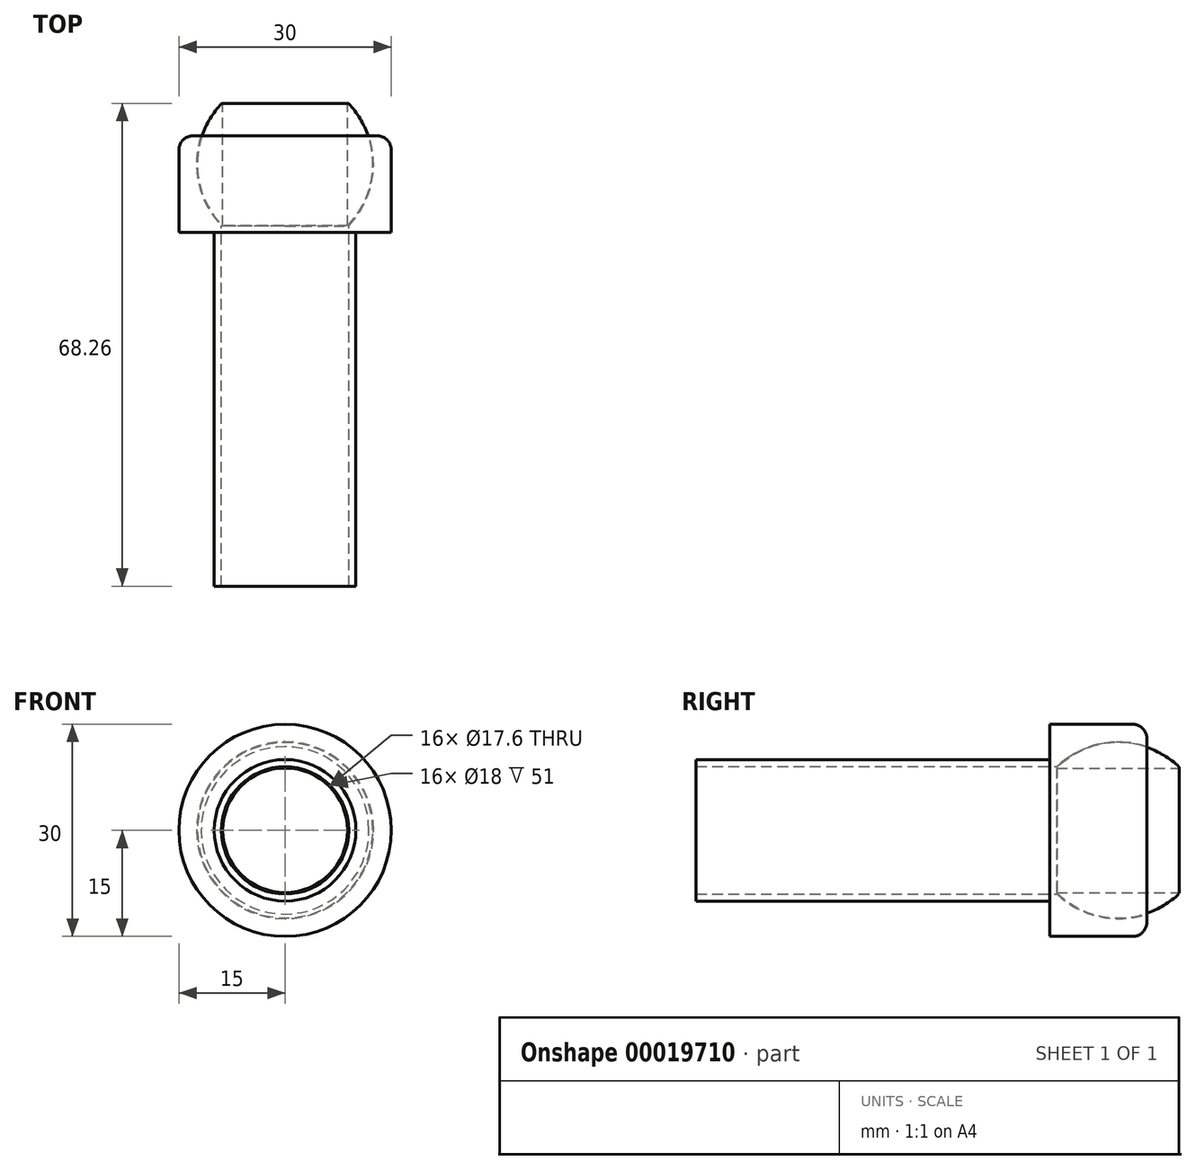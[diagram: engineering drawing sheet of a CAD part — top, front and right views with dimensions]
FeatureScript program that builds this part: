
annotation { "Feature Type Name" : "Feature", "Feature Type Description" : "" }
export const myFeature = defineFeature(function(context is Context, id is Id, definition is map)
    precondition{}
    {
        {
            var Q0;
            Q0=qCreatedBy(makeId("Top.planeOp"),FACE);
            var sketch = newSketch(context, id + "F0", { "sketchPlane" : qUnion([Q0])});
            skLineSegment(sketch, "E0", {"start": v(0, 31.42) * mm, "end": v(0, -28.3) * mm, "construction": true});
            skArc(sketch, "E1", {"start": v(9, 1) * mm, "mid": v(12.2, 6.95) * mm, "end": v(11.84, 13.69) * mm});
            skLineSegment(sketch, "E2", {"start": v(9, 0) * mm, "end": v(9, 1) * mm});
            skLineSegment(sketch, "E3", {"start": v(15, 0) * mm, "end": v(15, 13.69) * mm});
            skLineSegment(sketch, "E4", {"start": v(11.84, 13.69) * mm, "end": v(15, 13.69) * mm});
            skLineSegment(sketch, "E5", {"start": v(9, 0) * mm, "end": v(9, -50) * mm});
            skLineSegment(sketch, "E6", {"start": v(9, -50) * mm, "end": v(10, -50) * mm});
            skLineSegment(sketch, "E7", {"start": v(10, -50) * mm, "end": v(10, 0) * mm});
            skLineSegment(sketch, "E8", {"start": v(10, 0) * mm, "end": v(15, 0) * mm});
            skArc(sketch, "E9", {"start": v(8.8, 0.94) * mm, "mid": v(12.4, 9.67) * mm, "end": v(8.8, 18.41) * mm});
            skLineSegment(sketch, "E10", {"start": v(8.8, 19.95) * mm, "end": v(8.8, -2.87) * mm});
            skSolve(sketch);
        }
        {
            var Q0;
            Q0 = qSketchRegion(id + "F0", true);
            var Q1;
            Q1=sQuery(id+"F0.wireOp",EDGE,"E0");
            revolve(context, id + "F1", {"entities" : qUnion([Q0]), "axis" : qUnion([Q1]), "revolveType" : RevolveType.FULL});
        }
        {
            var Q0;
            Q0=makeQuery(id+"F1.opRevolve","SWEPT_EDGE",EDGE,{"disambiguationData":[OSD([sQuery(id+"F0.wireOp",EDGE,"E3"),sQuery(id+"F0.wireOp",EDGE,"E4")])]});
            fillet(context, id + "F2", {"entities" : qUnion([Q0]), "radius" : 2 * mm, "tangentPropagation" : true, "allowEdgeOverflow" : false});
        }
        {
            var Q0;
            {var subQ0=sQuery(id+"F0.wireOp",EDGE,"E9");var subQ1=sQuery(id+"F0.wireOp",EDGE,"E10");Q0=makeQuery(id+"F1.opRevolve","SWEPT_EDGE",EDGE,{"disambiguationData":[OSD([subQ0,subQ1]),TDD([makeQuery(id+"F0.imprint","INTERSECT",VERTEX,{"disambiguationData":[OD(1.0)],"derivedFrom":[subQ0,subQ1]})])]});}
            fillet(context, id + "F3", {"entities" : qUnion([Q0]), "radius" : 0.1 * mm, "tangentPropagation" : true, "allowEdgeOverflow" : false});
        }
    });
